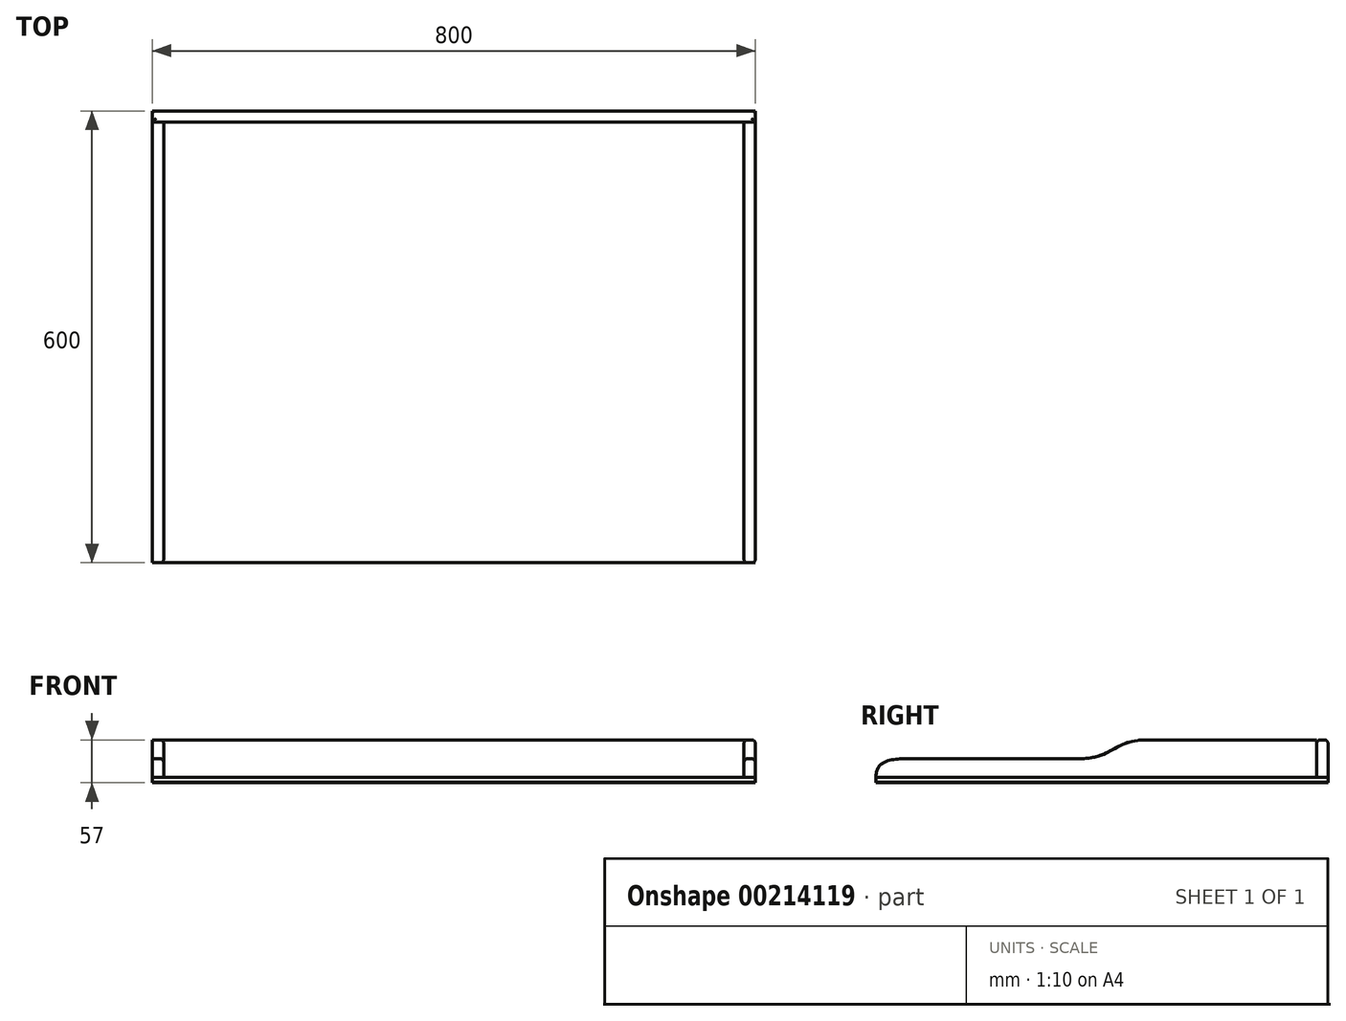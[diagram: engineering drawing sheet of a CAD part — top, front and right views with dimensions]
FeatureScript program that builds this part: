
annotation { "Feature Type Name" : "Feature", "Feature Type Description" : "" }
export const myFeature = defineFeature(function(context is Context, id is Id, definition is map)
    precondition{}
    {
        {
            assignVariable(context, id + "F0", {"name" : "Thickness", "anyValue" : 6});
        }
        {
            assignVariable(context, id + "F1", {"name" : "SideHeight", "anyValue" : 50});
        }
        {
            var Q0;
            Q0=qCreatedBy(makeId("Top.planeOp"),FACE);
            var sketch = newSketch(context, id + "F2", { "sketchPlane" : qUnion([Q0])});
            skLineSegment(sketch, "E0.bottom", {"start": v(400, -300) * mm, "end": v(-400, -300) * mm});
            skLineSegment(sketch, "E0.top", {"start": v(400, 300) * mm, "end": v(-400, 300) * mm});
            skLineSegment(sketch, "E0.left", {"start": v(400, -300) * mm, "end": v(400, 300) * mm});
            skLineSegment(sketch, "E0.right", {"start": v(-400, -300) * mm, "end": v(-400, 300) * mm});
            skPoint(sketch, "E0.middle", {"position": v(0, 0) * mm});
            skSolve(sketch);
        }
        {
            var Q0;
            Q0 = qSketchRegion(id + "F2", true);
            extrude(context, id + "F3", {"entities" : qUnion([Q0]), "depth" : (getVariable(context, 'Thickness')) * mm});
        }
        {
            var Q0;
            Q0=makeQuery(id+"F3.opExtrude","CAP_FACE",FACE,{"disambiguationData":[OSD([sQuery(id+"F2.wireOp",EDGE,"E0.bottom"),sQuery(id+"F2.wireOp",EDGE,"E0.top"),sQuery(id+"F2.wireOp",EDGE,"E0.left"),sQuery(id+"F2.wireOp",EDGE,"E0.right")])],"isStart":true});
            var sketch = newSketch(context, id + "F4", { "sketchPlane" : qUnion([Q0])});
            skLineSegment(sketch, "E1.bottom", {"start": v(-400, 300) * mm, "end": v(400, 300) * mm});
            skLineSegment(sketch, "E1.top", {"start": v(-400, -300) * mm, "end": v(400, -300) * mm});
            skLineSegment(sketch, "E1.left", {"start": v(-400, 300) * mm, "end": v(-400, -300) * mm});
            skLineSegment(sketch, "E1.right", {"start": v(400, 300) * mm, "end": v(400, -300) * mm});
            skSolve(sketch);
        }
        {
            var Q0;
            Q0 = qSketchRegion(id + "F4", true);
            extrude(context, id + "F5", {"entities" : qUnion([Q0]), "depth" : 1 * mm});
        }
        {
            var Q0;
            Q0=makeQuery(id+"F3.opExtrude","CAP_FACE",FACE,{"disambiguationData":[OSD([sQuery(id+"F2.wireOp",EDGE,"E0.bottom"),sQuery(id+"F2.wireOp",EDGE,"E0.top"),sQuery(id+"F2.wireOp",EDGE,"E0.left"),sQuery(id+"F2.wireOp",EDGE,"E0.right")])],"isStart":false});
            var sketch = newSketch(context, id + "F6", { "sketchPlane" : qUnion([Q0])});
            skLineSegment(sketch, "E2.bottom", {"start": v(-400, 300) * mm, "end": v(400, 300) * mm});
            skLineSegment(sketch, "E2.top", {"start": v(-400, 285) * mm, "end": v(400, 285) * mm});
            skLineSegment(sketch, "E2.left", {"start": v(-400, 300) * mm, "end": v(-400, 285) * mm});
            skLineSegment(sketch, "E2.right", {"start": v(400, 300) * mm, "end": v(400, 285) * mm});
            skSolve(sketch);
        }
        {
            var Q0;
            Q0 = qSketchRegion(id + "F6", true);
            extrude(context, id + "F7", {"entities" : qUnion([Q0]), "depth" : (getVariable(context, 'SideHeight')) * mm});
        }
        {
            var Q0;
            Q0=makeQuery(id+"F3.opExtrude","CAP_FACE",FACE,{"disambiguationData":[OSD([sQuery(id+"F2.wireOp",EDGE,"E0.bottom"),sQuery(id+"F2.wireOp",EDGE,"E0.top"),sQuery(id+"F2.wireOp",EDGE,"E0.left"),sQuery(id+"F2.wireOp",EDGE,"E0.right")])],"isStart":false});
            var sketch = newSketch(context, id + "F8", { "sketchPlane" : qUnion([Q0])});
            skLineSegment(sketch, "E3.bottom", {"start": v(-400, -300) * mm, "end": v(-385, -300) * mm});
            skLineSegment(sketch, "E3.top", {"start": v(-400, 285) * mm, "end": v(-385, 285) * mm});
            skLineSegment(sketch, "E3.left", {"start": v(-400, -300) * mm, "end": v(-400, 285) * mm});
            skLineSegment(sketch, "E3.right", {"start": v(-385, -300) * mm, "end": v(-385, 285) * mm});
            skLineSegment(sketch, "E4.bottom", {"start": v(400, -300) * mm, "end": v(385, -300) * mm});
            skLineSegment(sketch, "E4.top", {"start": v(400, 285) * mm, "end": v(385, 285) * mm});
            skLineSegment(sketch, "E4.left", {"start": v(400, -300) * mm, "end": v(400, 285) * mm});
            skLineSegment(sketch, "E4.right", {"start": v(385, -300) * mm, "end": v(385, 285) * mm});
            skSolve(sketch);
        }
        {
            var Q0;
            Q0 = qSketchRegion(id + "F8", true);
            extrude(context, id + "F9", {"entities" : qUnion([Q0]), "depth" : (getVariable(context, 'SideHeight')) * mm});
        }
        {
            var Q0;
            Q0=makeQuery(id+"F9.opExtrude","SWEPT_FACE",FACE,{"disambiguationData":[OSD([sQuery(id+"F8.wireOp",EDGE,"E3.left")])]});
            var sketch = newSketch(context, id + "F10", { "sketchPlane" : qUnion([Q0])});
            skFitSpline(sketch, "E5", {"points": [v(-60, 56) * mm, v(30, 31) * mm], "startDerivative": vector(135, 0) * mm, "endDerivative": vector(135, 0) * mm});
            skFitSpline(sketch, "E6", {"points": [v(300, 6) * mm, v(252, 31) * mm], "startDerivative": vector(0, 75) * mm, "endDerivative": vector(-72, 0) * mm});
            skLineSegment(sketch, "E7", {"start": v(30, 31) * mm, "end": v(252, 31) * mm});
            skLineSegment(sketch, "E8", {"start": v(-60, 56) * mm, "end": v(300, 56) * mm});
            skLineSegment(sketch, "E9", {"start": v(300, 56) * mm, "end": v(300, 6) * mm});
            skSolve(sketch);
        }
        {
            var Q0;
            Q0 = qSketchRegion(id + "F10", true);
            extrude(context, id + "F11", {"entities" : qUnion([Q0]), "operationType" : NewBodyOperationType.REMOVE, "endBound" : BoundingType.THROUGH_ALL, "oppositeDirection" : true, "depth" : 25 * mm});
        }
        {
            var Q0;
            Q0=makeQuery(id+"F11.boolean.opBoolean","COPY",EDGE,{"derivedFrom":makeQuery(id+"F11.opExtrude","CAP_EDGE",EDGE,{"disambiguationData":[OSD([sQuery(id+"F10.wireOp",EDGE,"E7")])],"isStart":true})});
            var Q1;
            Q1=makeQuery(id+"F11.boolean.opBoolean","COPY",EDGE,{"derivedFrom":makeQuery(id+"F11.opExtrude","CAP_EDGE",EDGE,{"disambiguationData":[OSD([sQuery(id+"F10.wireOp",EDGE,"E6")])],"isStart":true})});
            var Q2;
            Q2=makeQuery(id+"F11.boolean.opBoolean","INTERSECT",EDGE,{"derivedFrom":[makeQuery(id+"F9.opExtrude","SWEPT_FACE",FACE,{"disambiguationData":[OSD([sQuery(id+"F8.wireOp",EDGE,"E3.right")])]}),makeQuery(id+"F11.opExtrude","SWEPT_FACE",FACE,{"disambiguationData":[OSD([sQuery(id+"F10.wireOp",EDGE,"E7")])]})]});
            var Q3;
            Q3=makeQuery(id+"F11.boolean.opBoolean","INTERSECT",EDGE,{"derivedFrom":[makeQuery(id+"F9.opExtrude","SWEPT_FACE",FACE,{"disambiguationData":[OSD([sQuery(id+"F8.wireOp",EDGE,"E3.right")])]}),makeQuery(id+"F11.opExtrude","SWEPT_FACE",FACE,{"disambiguationData":[OSD([sQuery(id+"F10.wireOp",EDGE,"E6")])]})]});
            var Q4;
            Q4=makeQuery(id+"F11.boolean.opBoolean","INTERSECT",EDGE,{"derivedFrom":[makeQuery(id+"F9.opExtrude","SWEPT_FACE",FACE,{"disambiguationData":[OSD([sQuery(id+"F8.wireOp",EDGE,"E4.left")])]}),makeQuery(id+"F11.opExtrude","SWEPT_FACE",FACE,{"disambiguationData":[OSD([sQuery(id+"F10.wireOp",EDGE,"E7")])]})]});
            var Q5;
            Q5=makeQuery(id+"F11.boolean.opBoolean","INTERSECT",EDGE,{"derivedFrom":[makeQuery(id+"F9.opExtrude","SWEPT_FACE",FACE,{"disambiguationData":[OSD([sQuery(id+"F8.wireOp",EDGE,"E4.left")])]}),makeQuery(id+"F11.opExtrude","SWEPT_FACE",FACE,{"disambiguationData":[OSD([sQuery(id+"F10.wireOp",EDGE,"E6")])]})]});
            var Q6;
            Q6=makeQuery(id+"F11.boolean.opBoolean","INTERSECT",EDGE,{"derivedFrom":[makeQuery(id+"F9.opExtrude","SWEPT_FACE",FACE,{"disambiguationData":[OSD([sQuery(id+"F8.wireOp",EDGE,"E4.right")])]}),makeQuery(id+"F11.opExtrude","SWEPT_FACE",FACE,{"disambiguationData":[OSD([sQuery(id+"F10.wireOp",EDGE,"E6")])]})]});
            var Q7;
            Q7=makeQuery(id+"F11.boolean.opBoolean","INTERSECT",EDGE,{"derivedFrom":[makeQuery(id+"F9.opExtrude","SWEPT_FACE",FACE,{"disambiguationData":[OSD([sQuery(id+"F8.wireOp",EDGE,"E4.right")])]}),makeQuery(id+"F11.opExtrude","SWEPT_FACE",FACE,{"disambiguationData":[OSD([sQuery(id+"F10.wireOp",EDGE,"E7")])]})]});
            var Q8;
            Q8=makeQuery(id+"F7.opExtrude","CAP_EDGE",EDGE,{"disambiguationData":[OSD([sQuery(id+"F6.wireOp",EDGE,"E2.top")])],"isStart":false});
            var Q9;
            Q9=makeQuery(id+"F7.opExtrude","CAP_EDGE",EDGE,{"disambiguationData":[OSD([sQuery(id+"F6.wireOp",EDGE,"E2.bottom")])],"isStart":false});
            var Q10;
            Q10=makeQuery(id+"F7.opExtrude","SWEPT_EDGE",EDGE,{"disambiguationData":[OSD([sQuery(id+"F6.wireOp",EDGE,"E2.bottom"),sQuery(id+"F6.wireOp",EDGE,"E2.right")])]});
            var Q11;
            Q11=makeQuery(id+"F7.opExtrude","SWEPT_EDGE",EDGE,{"disambiguationData":[OSD([sQuery(id+"F6.wireOp",EDGE,"E2.bottom"),sQuery(id+"F6.wireOp",EDGE,"E2.left")])]});
            var Q12;
            Q12=makeQuery(id+"F7.opExtrude","CAP_EDGE",EDGE,{"disambiguationData":[OSD([sQuery(id+"F6.wireOp",EDGE,"E2.left")])],"isStart":false});
            var Q13;
            Q13=makeQuery(id+"F7.opExtrude","CAP_EDGE",EDGE,{"disambiguationData":[OSD([sQuery(id+"F6.wireOp",EDGE,"E2.right")])],"isStart":false});
            fillet(context, id + "F12", {"entities" : qUnion([Q0, Q1, Q2, Q3, Q4, Q5, Q6, Q7, Q8, Q9, Q10, Q11, Q12, Q13]), "radius" : 5 * mm, "tangentPropagation" : true, "allowEdgeOverflow" : false});
        }
    });
